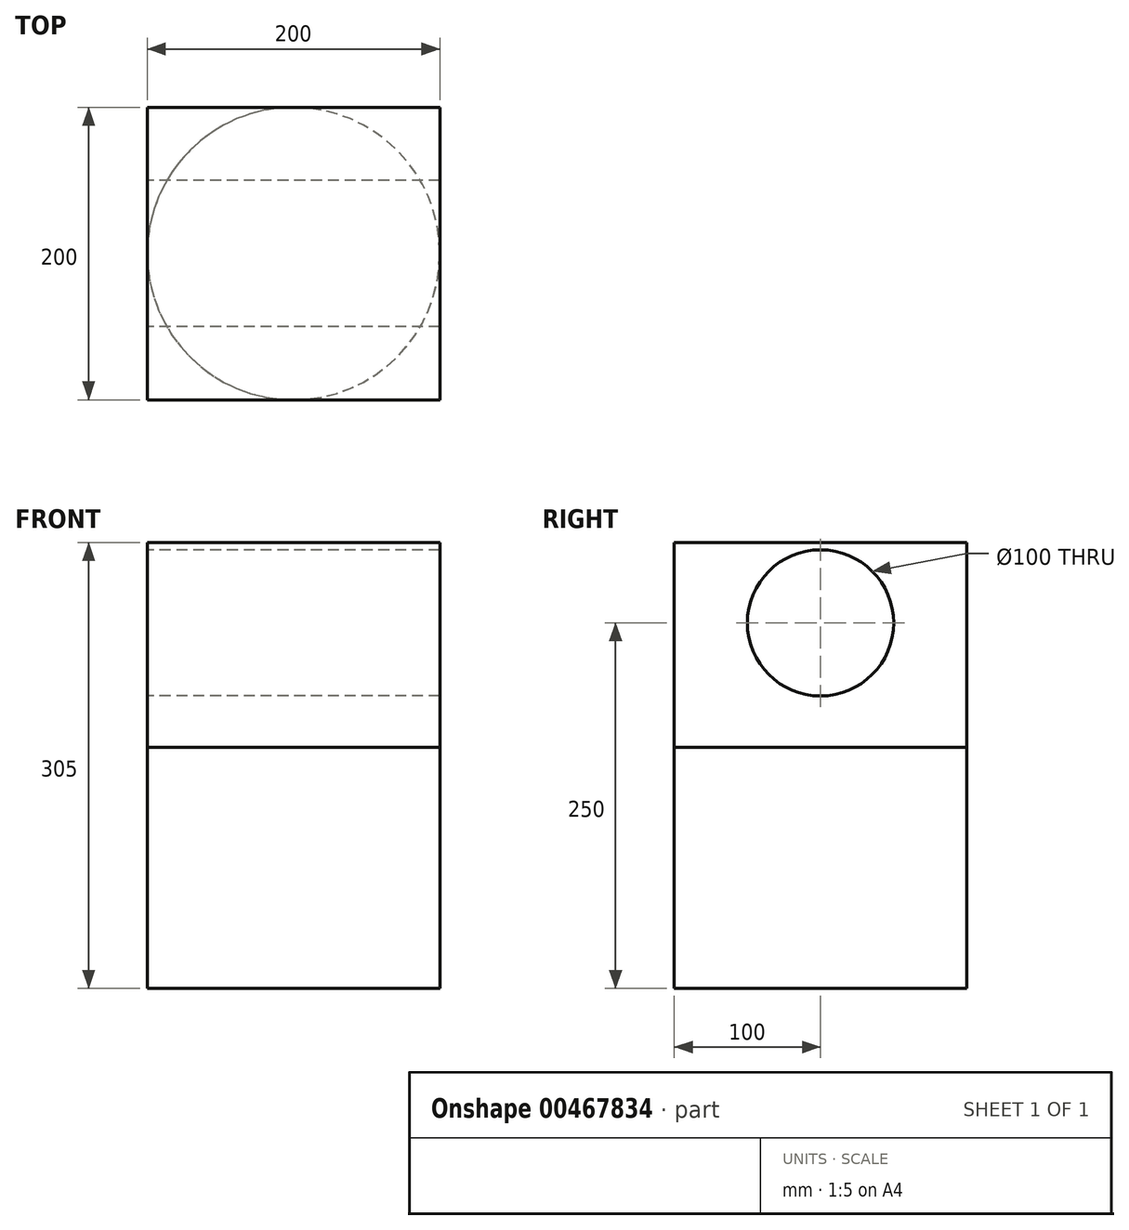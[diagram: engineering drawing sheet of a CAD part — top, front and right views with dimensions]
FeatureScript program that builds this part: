
annotation { "Feature Type Name" : "Feature", "Feature Type Description" : "" }
export const myFeature = defineFeature(function(context is Context, id is Id, definition is map)
    precondition{}
    {
        {
            var Q0;
            Q0=qCreatedBy(makeId("Top.planeOp"),FACE);
            var sketch = newSketch(context, id + "F0", { "sketchPlane" : qUnion([Q0])});
            skCircle(sketch, "E0", {"center": v(0, 0) * mm, "radius": 100 * mm});
            skSolve(sketch);
        }
        {
            var Q0;
            Q0 = qSketchRegion(id + "F0", true);
            extrude(context, id + "F1", {"entities" : qUnion([Q0]), "depth" : 265 * mm, "offsetDistance" : 25 * mm});
        }
        {
            var Q0;
            Q0=makeQuery(id+"F1.opExtrude","CAP_FACE",FACE,{"disambiguationData":[OSD([sQuery(id+"F0.wireOp",EDGE,"E0")])],"isStart":true});
            var sketch = newSketch(context, id + "F2", { "sketchPlane" : qUnion([Q0])});
            skCircle(sketch, "E1", {"center": v(0, 0) * mm, "radius": 100 * mm});
            skSolve(sketch);
        }
        {
            var Q0;
            Q0 = qSketchRegion(id + "F2", true);
            extrude(context, id + "F3", {"entities" : qUnion([Q0]), "operationType" : NewBodyOperationType.REMOVE, "oppositeDirection" : true, "depth" : 100 * mm, "offsetDistance" : 25 * mm});
        }
        {
            var Q0;
            Q0=makeQuery(id+"F1.opExtrude","CAP_FACE",FACE,{"disambiguationData":[OSD([sQuery(id+"F0.wireOp",EDGE,"E0")])],"isStart":false});
            var sketch = newSketch(context, id + "F4", { "sketchPlane" : qUnion([Q0])});
            skLineSegment(sketch, "E2.bottom", {"start": v(100, -100) * mm, "end": v(-100, -100) * mm});
            skLineSegment(sketch, "E2.top", {"start": v(100, 100) * mm, "end": v(-100, 100) * mm});
            skLineSegment(sketch, "E2.left", {"start": v(100, -100) * mm, "end": v(100, 100) * mm});
            skLineSegment(sketch, "E2.right", {"start": v(-100, -100) * mm, "end": v(-100, 100) * mm});
            skPoint(sketch, "E2.middle", {"position": v(0, 0) * mm});
            skSolve(sketch);
        }
        {
            var Q0;
            Q0 = qSketchRegion(id + "F4", true);
            extrude(context, id + "F5", {"entities" : qUnion([Q0]), "operationType" : NewBodyOperationType.ADD, "depth" : 140 * mm, "offsetDistance" : 25 * mm});
        }
        {
            var Q0;
            Q0=makeQuery(id+"F5.opExtrude","SWEPT_FACE",FACE,{"disambiguationData":[OSD([sQuery(id+"F4.wireOp",EDGE,"E2.right")])]});
            var sketch = newSketch(context, id + "F6", { "sketchPlane" : qUnion([Q0])});
            skCircle(sketch, "E3", {"center": v(0, 350) * mm, "radius": 50 * mm});
            skSolve(sketch);
        }
        {
            var Q0;
            Q0 = qSketchRegion(id + "F6", true);
            extrude(context, id + "F7", {"entities" : qUnion([Q0]), "operationType" : NewBodyOperationType.REMOVE, "oppositeDirection" : true, "depth" : 200 * mm, "offsetDistance" : 25 * mm});
        }
    });
